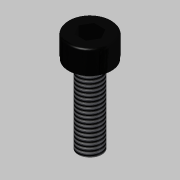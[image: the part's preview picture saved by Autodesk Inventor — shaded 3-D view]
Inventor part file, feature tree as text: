
AUTODESK INVENTOR PART (.ipt)
format: ipt  version: 2014 (Build 180170000, 170)  size: 117,248 bytes
history: native  units: mm
features: extrude x4, sketch x4, fillet x1, thread x1, reference x1
ambient origin geometry x8: Origin, YZ Plane, XZ Plane, XY Plane, X Axis, Y Axis, Z Axis, Center Point
bodies: Solid1 (feature_tree)
feature tree (11):
  extrude  "Extrusion1"  Depth=10.0mm TaperAngle=0.0deg
  extrude  "Extrusion2"  Depth=3.0mm TaperAngle=0.0deg
  fillet  "Fillet1"  Radius=0.3mm
  extrude  "Extrusion3"  Depth=0.5mm TaperAngle=0.0deg
  extrude  "Extrusion4"  Depth=2.0mm TaperAngle=0.0deg
  thread  "Thread1"  [1 undecoded]
  sketch  "Sketch1"  dims[d0=3.0mm d1=10.0mm d2=0.0mm]
  reference  "Reference1"
  sketch  "Sketch2"  dims[d3=5.6mm d4=3.0mm d5=0.0mm d6=0.3mm]
  sketch  "Sketch3"  dims[d7=5.5mm d8=0.5mm d9=0.0mm]
  sketch  "Sketch4"  dims[d10=2.5mm d11=2.0mm d12=0.0mm d13=10.0mm d14=0.0mm]
note: 1 required parameter value undecoded (feature->parameter linkage not recoverable at this tier; creation-order binding heuristic only, values carry confidence <= 0.55)
